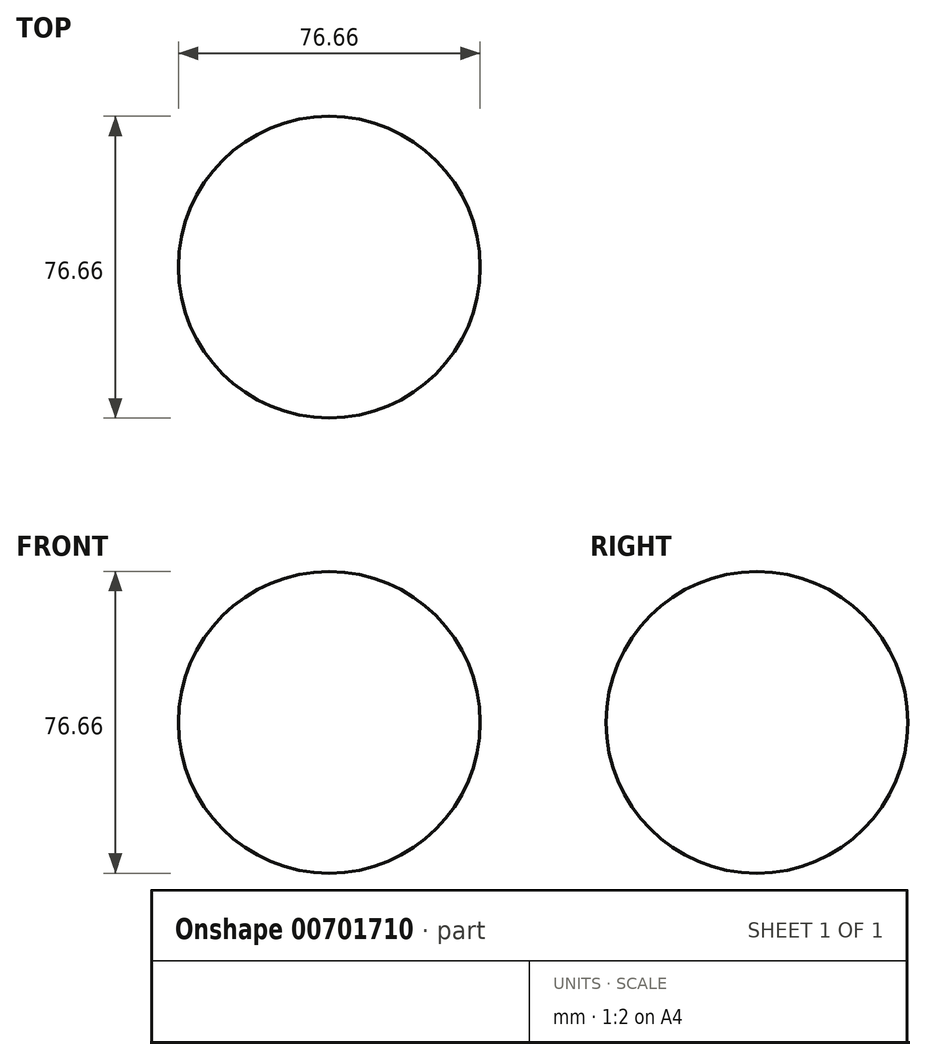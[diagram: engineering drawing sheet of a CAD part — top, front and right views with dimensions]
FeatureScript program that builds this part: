
annotation { "Feature Type Name" : "Feature", "Feature Type Description" : "" }
export const myFeature = defineFeature(function(context is Context, id is Id, definition is map)
    precondition{}
    {
        {
            var Q0;
            Q0=qCreatedBy(makeId("Front.planeOp"),FACE);
            var sketch = newSketch(context, id + "F0", { "sketchPlane" : qUnion([Q0])});
            skArc(sketch, "E0", {"start": v(38.33, 0) * mm, "mid": v(0, 38.33) * mm, "end": v(-38.33, 0) * mm});
            skLineSegment(sketch, "E1", {"start": v(-38.33, 0) * mm, "end": v(38.33, 0) * mm});
            skSolve(sketch);
        }
        {
            var Q0;
            Q0=sQuery(id+"F0.wireOp",EDGE,"E0");
            var Q1;
            Q1=sQuery(id+"F0.wireOp",EDGE,"E1");
            revolve(context, id + "F1", {"bodyType" : ToolBodyType.SURFACE, "surfaceOperationType" : NewSurfaceOperationType.NEW, "surfaceEntities" : qUnion([Q0]), "axis" : qUnion([Q1]), "revolveType" : RevolveType.FULL});
        }
    });
